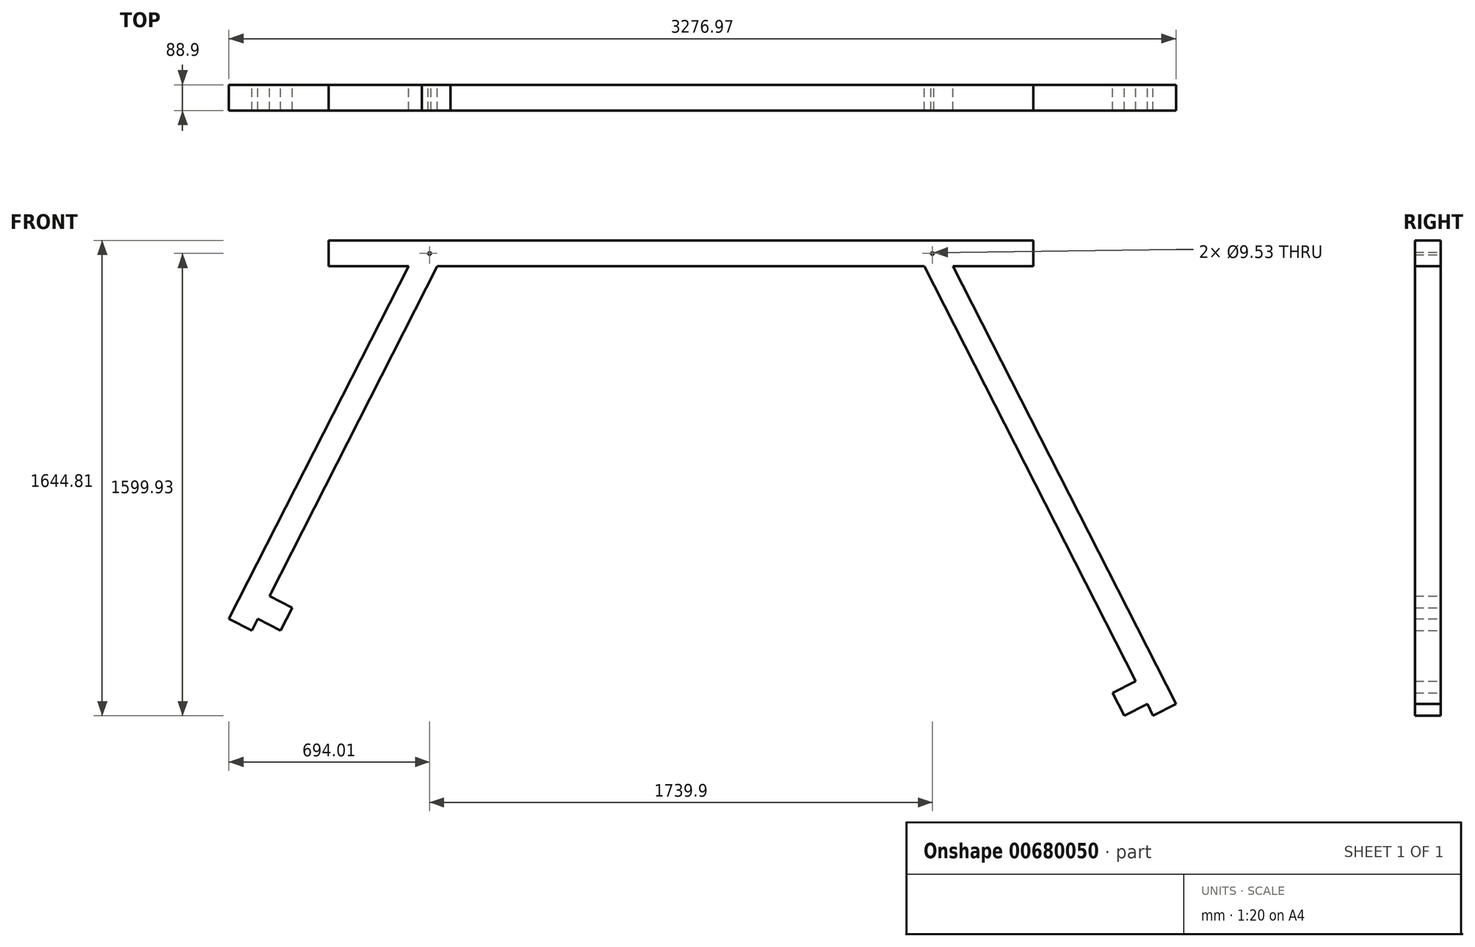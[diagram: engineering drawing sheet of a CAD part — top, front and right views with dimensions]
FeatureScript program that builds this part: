
annotation { "Feature Type Name" : "Feature", "Feature Type Description" : "" }
export const myFeature = defineFeature(function(context is Context, id is Id, definition is map)
    precondition{}
    {
        {
            var Q0;
            Q0=qCreatedBy(makeId("Front.planeOp"),FACE);
            var sketch = newSketch(context, id + "F0", { "sketchPlane" : qUnion([Q0])});
            skLineSegment(sketch, "E0", {"start": v(-1563.96, 41.11) * mm, "end": v(-1484.75, 0.75) * mm});
            skLineSegment(sketch, "E1", {"start": v(-1484.75, 0.75) * mm, "end": v(-797.2, 1350.16) * mm});
            skLineSegment(sketch, "E2", {"start": v(-797.2, 1350.16) * mm, "end": v(-896.97, 1350.16) * mm});
            skLineSegment(sketch, "E3", {"start": v(-896.97, 1350.16) * mm, "end": v(-1563.96, 41.11) * mm});
            skLineSegment(sketch, "E4.bottom", {"start": v(-1424.2, 119.57) * mm, "end": v(-1345, 79.21) * mm});
            skLineSegment(sketch, "E4.top", {"start": v(-1464.57, 40.36) * mm, "end": v(-1385.36, 0) * mm});
            skLineSegment(sketch, "E4.left", {"start": v(-1424.2, 119.57) * mm, "end": v(-1464.57, 40.36) * mm});
            skLineSegment(sketch, "E4.right", {"start": v(-1345, 79.21) * mm, "end": v(-1385.36, 0) * mm});
            skCircle(sketch, "E5", {"center": v(-869.95, 1305.28) * mm, "radius": 4.76 * mm});
            skLineSegment(sketch, "E6.MirrorCS", {"start": v(1713.01, -253.53) * mm, "end": v(1633.8, -293.9) * mm});
            skCircle(sketch, "E7.MirrorC", {"center": v(869.95, 1305.28) * mm, "radius": 4.76 * mm});
            skLineSegment(sketch, "E8.MirrorCS", {"start": v(896.11, 1349.73) * mm, "end": v(1713.01, -253.53) * mm});
            skLineSegment(sketch, "E9.MirrorCS", {"start": v(796.34, 1349.73) * mm, "end": v(896.11, 1349.73) * mm});
            skLineSegment(sketch, "E10.MirrorCS", {"start": v(1633.8, -293.9) * mm, "end": v(796.34, 1349.73) * mm});
            skLineSegment(sketch, "E11.bottom", {"start": v(-1219.2, 1349.73) * mm, "end": v(1219.2, 1349.73) * mm});
            skLineSegment(sketch, "E11.top", {"start": v(-1219.2, 1260.83) * mm, "end": v(1219.2, 1260.83) * mm});
            skLineSegment(sketch, "E11.left", {"start": v(-1219.2, 1349.73) * mm, "end": v(-1219.2, 1260.83) * mm});
            skLineSegment(sketch, "E11.right", {"start": v(1219.2, 1349.73) * mm, "end": v(1219.2, 1260.83) * mm});
            skLineSegment(sketch, "E12", {"start": v(796.34, 1349.73) * mm, "end": v(892.04, 1398.5) * mm, "construction": true});
            skLineSegment(sketch, "E13", {"start": v(-1385.36, 0) * mm, "end": v(1534.41, -294.65) * mm, "construction": true});
            skLineSegment(sketch, "E14", {"start": v(-797.2, 1350.16) * mm, "end": v(-909.28, 1407.27) * mm, "construction": true});
            skLineSegment(sketch, "E15.bottom", {"start": v(1494.05, -215.44) * mm, "end": v(1573.26, -175.08) * mm});
            skLineSegment(sketch, "E15.top", {"start": v(1534.41, -294.65) * mm, "end": v(1613.62, -254.29) * mm});
            skLineSegment(sketch, "E15.left", {"start": v(1494.05, -215.44) * mm, "end": v(1534.41, -294.65) * mm});
            skLineSegment(sketch, "E15.right", {"start": v(1573.26, -175.08) * mm, "end": v(1613.62, -254.29) * mm});
            skLineSegment(sketch, "E16", {"start": v(1534.41, -294.65) * mm, "end": v(1534.41, 0) * mm, "construction": true});
            skLineSegment(sketch, "E17", {"start": v(-1385.36, 0) * mm, "end": v(1534.41, 0) * mm, "construction": true});
            skSolve(sketch);
        }
        {
            var Q0;
            Q0 = qSketchRegion(id + "F0", true);
            extrude(context, id + "F1", {"entities" : qUnion([Q0]), "depth" : 88.9 * mm, "offsetDistance" : 25.4 * mm});
        }
    });
